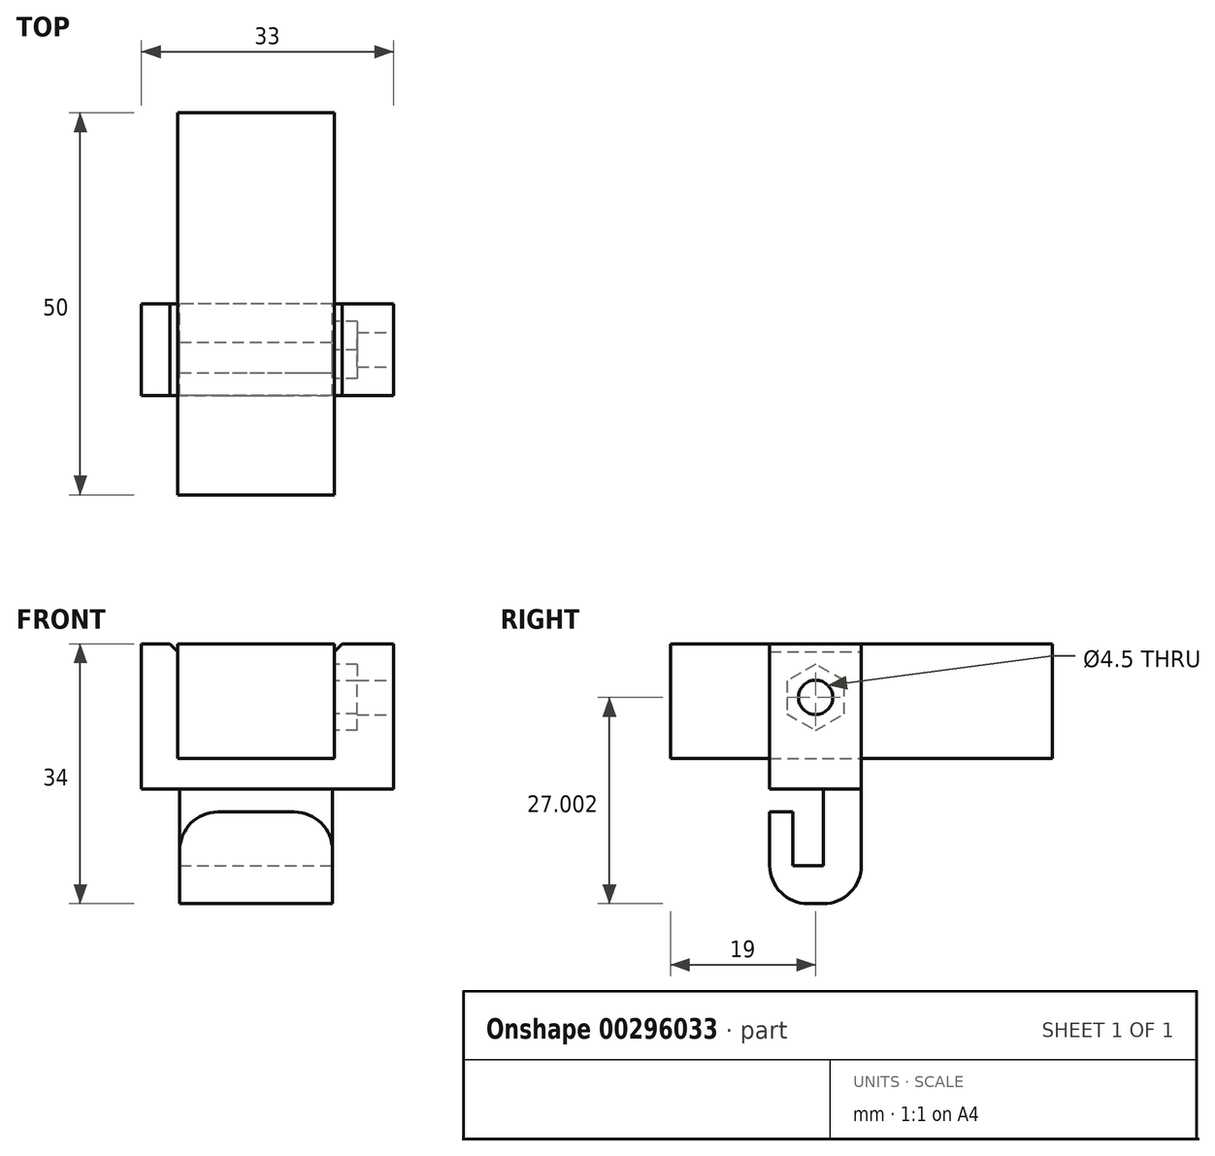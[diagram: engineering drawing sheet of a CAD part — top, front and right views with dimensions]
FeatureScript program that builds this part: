
annotation { "Feature Type Name" : "Feature", "Feature Type Description" : "" }
export const myFeature = defineFeature(function(context is Context, id is Id, definition is map)
    precondition{}
    {
        {
            var Q0;
            Q0=qCreatedBy(makeId("Front.planeOp"),FACE);
            var sketch = newSketch(context, id + "F0", { "sketchPlane" : qUnion([Q0])});
            skLineSegment(sketch, "E0.bottom", {"start": v(-10.25, 24.4) * mm, "end": v(10.25, 24.4) * mm});
            skLineSegment(sketch, "E0.top", {"start": v(-10.25, 9.4) * mm, "end": v(10.25, 9.4) * mm});
            skLineSegment(sketch, "E0.left", {"start": v(-10.25, 24.4) * mm, "end": v(-10.25, 9.4) * mm});
            skLineSegment(sketch, "E0.right", {"start": v(10.25, 24.4) * mm, "end": v(10.25, 9.4) * mm});
            skPoint(sketch, "E1", {"position": v(0, 24.4) * mm});
            skSolve(sketch);
        }
        {
            var Q0;
            Q0=makeQuery(id+"F0.imprint","IMPRINT",FACE,{"disambiguationData":[TD([[makeQuery(id+"F0.imprint","IMPRINT",EDGE,{"derivedFrom":sQuery(id+"F0.wireOp",EDGE,"E0.bottom")}),-1.0]])]});
            extrude(context, id + "F1", {"entities" : qUnion([Q0]), "depth" : 25 * mm, "hasSecondDirection" : true, "secondDirectionOppositeDirection" : true, "secondDirectionDepth" : 25 * mm});
        }
        {
            var Q0;
            Q0=qCreatedBy(makeId("Front.planeOp"),FACE);
            var sketch = newSketch(context, id + "F2", { "sketchPlane" : qUnion([Q0])});
            skLineSegment(sketch, "E2", {"start": v(-51.09, 24.4) * mm, "end": v(48.91, 24.4) * mm, "construction": true});
            skLineSegment(sketch, "E3.bottom", {"start": v(-15, 24.4) * mm, "end": v(18, 24.4) * mm});
            skLineSegment(sketch, "E3.top", {"start": v(-15, 5.4) * mm, "end": v(18, 5.4) * mm});
            skLineSegment(sketch, "E3.left", {"start": v(-15, 24.4) * mm, "end": v(-15, 5.4) * mm});
            skLineSegment(sketch, "E3.right", {"start": v(18, 24.4) * mm, "end": v(18, 5.4) * mm});
            skLineSegment(sketch, "E4", {"start": v(10.25, 24.4) * mm, "end": v(10.25, 9.4) * mm});
            skLineSegment(sketch, "E5", {"start": v(10.25, 9.4) * mm, "end": v(-10.25, 9.4) * mm});
            skLineSegment(sketch, "E6", {"start": v(-10.25, 9.4) * mm, "end": v(-10.25, 24.4) * mm});
            skSolve(sketch);
        }
        {
            var Q0;
            Q0=makeQuery(id+"F2.imprint","IMPRINT",FACE,{"disambiguationData":[TD([[makeQuery(id+"F2.imprint","IMPRINT",EDGE,{"derivedFrom":sQuery(id+"F2.wireOp",EDGE,"E3.bottom")}),-1.0]])]});
            extrude(context, id + "F3", {"entities" : qUnion([Q0]), "depth" : 12 * mm});
        }
        {
            var Q0;
            Q0=makeQuery(id+"F3.opExtrude","SWEPT_FACE",FACE,{"disambiguationData":[OSD([sQuery(id+"F2.wireOp",EDGE,"E3.right")])]});
            var sketch = newSketch(context, id + "F4", { "sketchPlane" : qUnion([Q0])});
            skCircle(sketch, "E7", {"center": v(-6, 17.4) * mm, "radius": 2.25 * mm});
            skSolve(sketch);
        }
        {
            var Q0;
            Q0=makeQuery(id+"F4.imprint","IMPRINT",FACE,{"disambiguationData":[TD([[makeQuery(id+"F4.imprint","IMPRINT",EDGE,{"derivedFrom":sQuery(id+"F4.wireOp",EDGE,"E7")}),1.0]])]});
            var Q1;
            Q1=makeQuery(id+"F3.opExtrude","SWEPT_FACE",FACE,{"disambiguationData":[OSD([sQuery(id+"F2.wireOp",EDGE,"E4")])]});
            extrude(context, id + "F5", {"entities" : qUnion([Q0]), "operationType" : NewBodyOperationType.REMOVE, "endBound" : BoundingType.UP_TO_SURFACE, "oppositeDirection" : true, "endBoundEntityFace" : qUnion([Q1]), "depth" : 25 * mm});
        }
        {
            var Q0;
            Q0=makeQuery(id+"F3.opExtrude","SWEPT_FACE",FACE,{"disambiguationData":[OSD([sQuery(id+"F2.wireOp",EDGE,"E4")])]});
            var sketch = newSketch(context, id + "F6", { "sketchPlane" : qUnion([Q0])});
            skCircle(sketch, "E8.cCircle", {"center": v(6, 17.4) * mm, "radius": 3.75 * mm, "construction": true});
            skLineSegment(sketch, "E8.0", {"start": v(6, 21.73) * mm, "end": v(9.75, 19.57) * mm});
            skLineSegment(sketch, "E8.1", {"start": v(9.75, 19.57) * mm, "end": v(9.75, 15.24) * mm});
            skLineSegment(sketch, "E8.2", {"start": v(9.75, 15.24) * mm, "end": v(6, 13.07) * mm});
            skLineSegment(sketch, "E8.3", {"start": v(6, 13.07) * mm, "end": v(2.25, 15.24) * mm});
            skLineSegment(sketch, "E8.4", {"start": v(2.25, 15.24) * mm, "end": v(2.25, 19.57) * mm});
            skLineSegment(sketch, "E8.5", {"start": v(2.25, 19.57) * mm, "end": v(6, 21.73) * mm});
            skPoint(sketch, "E8.0.midPoint", {"position": v(7.88, 20.65) * mm});
            skSolve(sketch);
        }
        {
            var Q0;
            Q0=makeQuery(id+"F6.imprint","IMPRINT",FACE,{"disambiguationData":[TD([[makeQuery(id+"F6.imprint","IMPRINT",EDGE,{"derivedFrom":sQuery(id+"F6.wireOp",EDGE,"E8.0")}),-1.0]])]});
            extrude(context, id + "F7", {"entities" : qUnion([Q0]), "operationType" : NewBodyOperationType.REMOVE, "oppositeDirection" : true, "depth" : 3 * mm});
        }
        {
            var Q0;
            Q0=makeQuery(id+"F3.opExtrude","SWEPT_EDGE",EDGE,{"disambiguationData":[OSD([sQuery(id+"F2.wireOp",EDGE,"E3.bottom"),sQuery(id+"F2.wireOp",EDGE,"E4")])]});
            var Q1;
            Q1=makeQuery(id+"F3.opExtrude","SWEPT_EDGE",EDGE,{"disambiguationData":[OSD([sQuery(id+"F2.wireOp",EDGE,"E3.bottom"),sQuery(id+"F2.wireOp",EDGE,"E6")])]});
            chamfer(context, id + "F8", {"entities" : qUnion([Q0, Q1]), "width" : 1 * mm, "tangentPropagation" : true});
        }
        {
            var Q0;
            Q0=makeQuery(id+"F3.opExtrude","CAP_FACE",FACE,{"disambiguationData":[OSD([sQuery(id+"F2.wireOp",EDGE,"E3.bottom"),sQuery(id+"F2.wireOp",EDGE,"E3.top"),sQuery(id+"F2.wireOp",EDGE,"E3.left"),sQuery(id+"F2.wireOp",EDGE,"E3.right"),sQuery(id+"F2.wireOp",EDGE,"E4"),sQuery(id+"F2.wireOp",EDGE,"E5"),sQuery(id+"F2.wireOp",EDGE,"E6")])],"isStart":true});
            var sketch = newSketch(context, id + "F9", { "sketchPlane" : qUnion([Q0])});
            skLineSegment(sketch, "E9.bottom", {"start": v(-10, 5.4) * mm, "end": v(10, 5.4) * mm});
            skLineSegment(sketch, "E9.top", {"start": v(-10, -9.6) * mm, "end": v(10, -9.6) * mm});
            skLineSegment(sketch, "E9.left", {"start": v(-10, 5.4) * mm, "end": v(-10, -9.6) * mm});
            skLineSegment(sketch, "E9.right", {"start": v(10, 5.4) * mm, "end": v(10, -9.6) * mm});
            skPoint(sketch, "E9.middle", {"position": v(0, 0) * mm});
            skPoint(sketch, "E10", {"position": v(0, -9.6) * mm});
            skSolve(sketch);
        }
        {
            var Q0;
            Q0=makeQuery(id+"F9.imprint","IMPRINT",FACE,{"disambiguationData":[TD([[makeQuery(id+"F9.imprint","IMPRINT",EDGE,{"derivedFrom":sQuery(id+"F9.wireOp",EDGE,"E9.bottom")}),1.0]])]});
            extrude(context, id + "F10", {"entities" : qUnion([Q0]), "operationType" : NewBodyOperationType.ADD, "oppositeDirection" : true, "depth" : 5 * mm});
        }
        {
            var Q0;
            Q0=makeQuery(id+"F10.opExtrude","CAP_FACE",FACE,{"disambiguationData":[OSD([sQuery(id+"F9.wireOp",EDGE,"E9.bottom"),sQuery(id+"F9.wireOp",EDGE,"E9.top"),sQuery(id+"F9.wireOp",EDGE,"E9.left"),sQuery(id+"F9.wireOp",EDGE,"E9.right")])],"isStart":false});
            var sketch = newSketch(context, id + "F11", { "sketchPlane" : qUnion([Q0])});
            skLineSegment(sketch, "E11.bottom", {"start": v(-10, -9.6) * mm, "end": v(10, -9.6) * mm});
            skLineSegment(sketch, "E11.top", {"start": v(-10, -4.6) * mm, "end": v(10, -4.6) * mm});
            skLineSegment(sketch, "E11.left", {"start": v(-10, -9.6) * mm, "end": v(-10, -4.6) * mm});
            skLineSegment(sketch, "E11.right", {"start": v(10, -9.6) * mm, "end": v(10, -4.6) * mm});
            skSolve(sketch);
        }
        {
            var Q0;
            Q0=makeQuery(id+"F11.imprint","IMPRINT",FACE,{"disambiguationData":[TD([[makeQuery(id+"F11.imprint","IMPRINT",EDGE,{"derivedFrom":sQuery(id+"F11.wireOp",EDGE,"E11.bottom")}),-1.0]])]});
            extrude(context, id + "F12", {"entities" : qUnion([Q0]), "operationType" : NewBodyOperationType.ADD, "depth" : 7 * mm});
        }
        {
            var Q0;
            Q0=makeQuery(id+"F12.opExtrude","SWEPT_FACE",FACE,{"disambiguationData":[OSD([sQuery(id+"F11.wireOp",EDGE,"E11.top")])]});
            var sketch = newSketch(context, id + "F13", { "sketchPlane" : qUnion([Q0])});
            skLineSegment(sketch, "E12.bottom", {"start": v(-10, -12) * mm, "end": v(10, -12) * mm});
            skLineSegment(sketch, "E12.top", {"start": v(-10, -9) * mm, "end": v(10, -9) * mm});
            skLineSegment(sketch, "E12.left", {"start": v(-10, -12) * mm, "end": v(-10, -9) * mm});
            skLineSegment(sketch, "E12.right", {"start": v(10, -12) * mm, "end": v(10, -9) * mm});
            skSolve(sketch);
        }
        {
            var Q0;
            Q0=makeQuery(id+"F13.imprint","IMPRINT",FACE,{"disambiguationData":[TD([[makeQuery(id+"F13.imprint","IMPRINT",EDGE,{"derivedFrom":sQuery(id+"F13.wireOp",EDGE,"E12.bottom")}),1.0]])]});
            extrude(context, id + "F14", {"entities" : qUnion([Q0]), "operationType" : NewBodyOperationType.ADD, "depth" : 7 * mm});
        }
        {
            var Q0;
            Q0=makeQuery(id+"F10.opExtrude","CAP_EDGE",EDGE,{"disambiguationData":[OSD([sQuery(id+"F9.wireOp",EDGE,"E9.top")])],"isStart":true});
            var Q1;
            Q1=makeQuery(id+"F12.opExtrude","CAP_EDGE",EDGE,{"disambiguationData":[OSD([sQuery(id+"F11.wireOp",EDGE,"E11.bottom")])],"isStart":false});
            var Q2;
            Q2=makeQuery(id+"F14.opExtrude","CAP_EDGE",EDGE,{"disambiguationData":[OSD([sQuery(id+"F13.wireOp",EDGE,"E12.right")])],"isStart":false});
            var Q3;
            Q3=makeQuery(id+"F14.opExtrude","CAP_EDGE",EDGE,{"disambiguationData":[OSD([sQuery(id+"F13.wireOp",EDGE,"E12.left")])],"isStart":false});
            var Q4;
            Q4=makeQuery(id+"F10.opExtrude","SWEPT_EDGE",EDGE,{"disambiguationData":[OSD([sQuery(id+"F2.wireOp",EDGE,"E3.top"),sQuery(id+"F9.wireOp",EDGE,"E9.bottom"),sQuery(id+"F9.wireOp",EDGE,"E9.left")])]});
            var Q5;
            Q5=makeQuery(id+"F10.opExtrude","SWEPT_EDGE",EDGE,{"disambiguationData":[OSD([sQuery(id+"F2.wireOp",EDGE,"E3.top"),sQuery(id+"F9.wireOp",EDGE,"E9.bottom"),sQuery(id+"F9.wireOp",EDGE,"E9.right")])]});
            fillet(context, id + "F15", {"entities" : qUnion([Q0, Q1, Q2, Q3, Q4, Q5]), "radius" : 5 * mm, "tangentPropagation" : true, "allowEdgeOverflow" : false});
        }
    });
